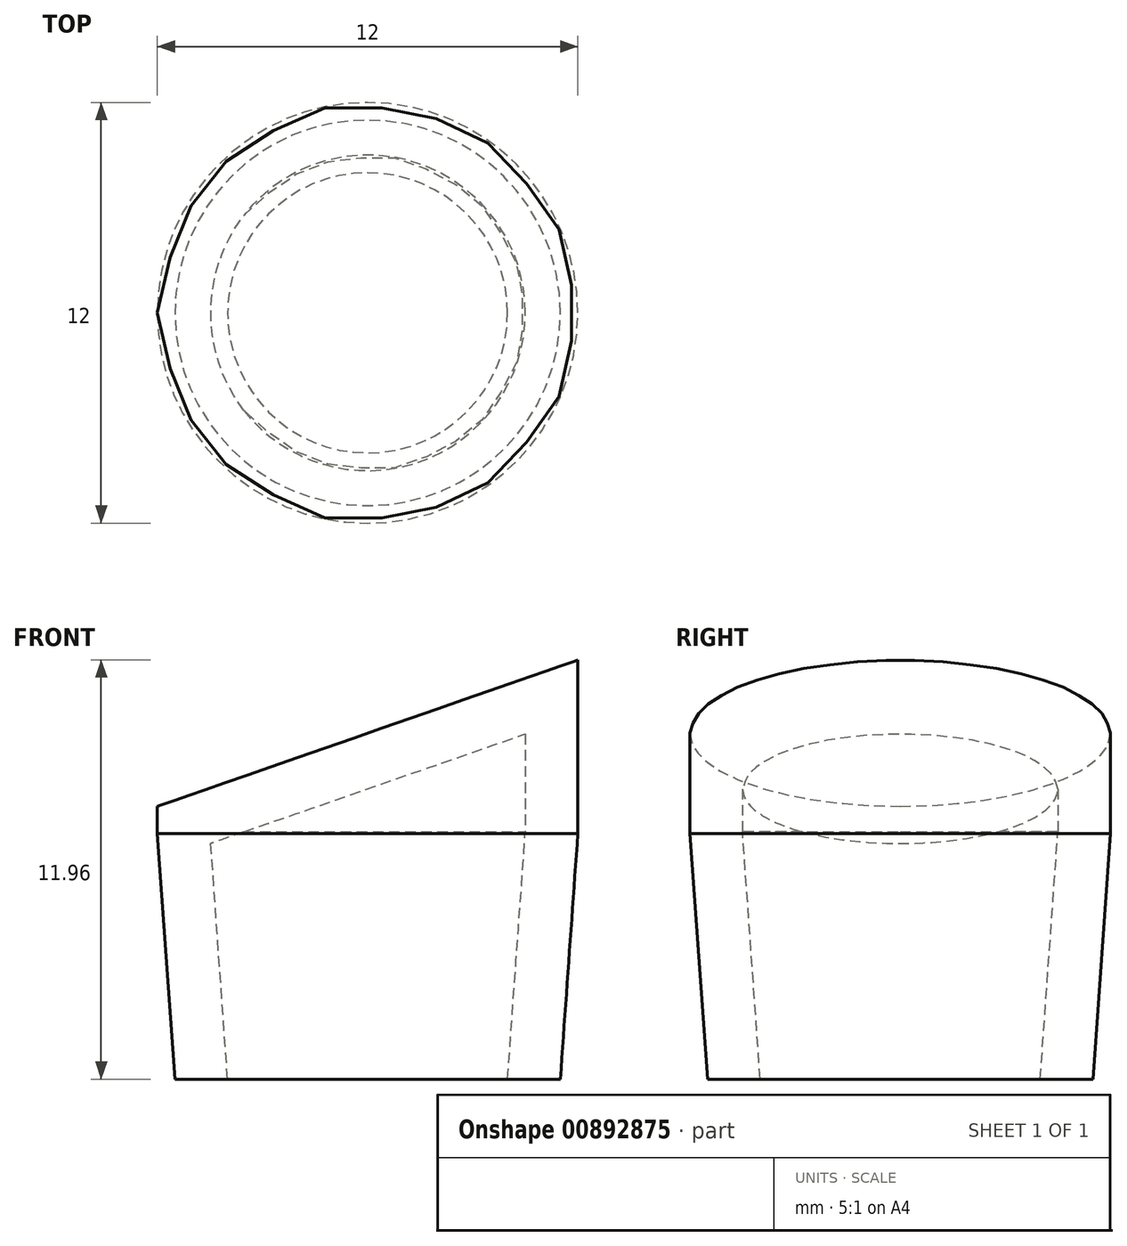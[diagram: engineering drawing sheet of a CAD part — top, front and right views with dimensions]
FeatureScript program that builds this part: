
annotation { "Feature Type Name" : "Feature", "Feature Type Description" : "" }
export const myFeature = defineFeature(function(context is Context, id is Id, definition is map)
    precondition{}
    {
        {
            var Q0;
            Q0=qCreatedBy(makeId("Top.planeOp"),FACE);
            var sketch = newSketch(context, id + "F0", { "sketchPlane" : qUnion([Q0])});
            skCircle(sketch, "E0", {"center": v(0, 0) * mm, "radius": 6 * mm});
            skSolve(sketch);
        }
        {
            var Q0;
            Q0 = qSketchRegion(id + "F0", true);
            extrude(context, id + "F1", {"entities" : qUnion([Q0]), "depth" : 12 * mm, "offsetDistance" : 25 * mm});
        }
        {
            var Q0;
            Q0=qCreatedBy(makeId("Front.planeOp"),FACE);
            var sketch = newSketch(context, id + "F2", { "sketchPlane" : qUnion([Q0])});
            skLineSegment(sketch, "E1", {"start": v(-8.25, 0) * mm, "end": v(-8.25, 7) * mm});
            skLineSegment(sketch, "E2", {"start": v(-8.25, 7) * mm, "end": v(7.9, 12.61) * mm});
            skLineSegment(sketch, "E3", {"start": v(7.9, 12.61) * mm, "end": v(-8.53, 16.3) * mm});
            skLineSegment(sketch, "E4", {"start": v(-8.53, 16.3) * mm, "end": v(-9.42, 8) * mm});
            skLineSegment(sketch, "E5", {"start": v(-9.42, 8) * mm, "end": v(-8.25, 7) * mm});
            skSolve(sketch);
        }
        {
            var Q0;
            Q0 = qSketchRegion(id + "F2", true);
            extrude(context, id + "F3", {"entities" : qUnion([Q0]), "operationType" : NewBodyOperationType.REMOVE, "oppositeDirection" : true, "depth" : 25 * mm, "offsetDistance" : 25 * mm, "hasSecondDirection" : true, "secondDirectionOppositeDirection" : false, "secondDirectionDepth" : 25 * mm});
        }
        {
            var Q0;
            Q0=makeQuery(id+"F1.opExtrude","CAP_EDGE",EDGE,{"disambiguationData":[OSD([sQuery(id+"F0.wireOp",EDGE,"E0")])],"isStart":true});
            chamfer(context, id + "F4", {"entities" : qUnion([Q0]), "chamferType" : ChamferType.TWO_OFFSETS, "width1" : 0.5 * mm, "oppositeDirection" : true, "width2" : 7 * mm, "tangentPropagation" : true});
        }
        {
            var Q0;
            Q0=makeQuery(id+"F1.opExtrude","CAP_FACE",FACE,{"disambiguationData":[OSD([sQuery(id+"F0.wireOp",EDGE,"E0")])],"isStart":true});
            shell(context, id + "F5", {"entities" : qUnion([Q0]), "thickness" : 1.5 * mm});
        }
    });
